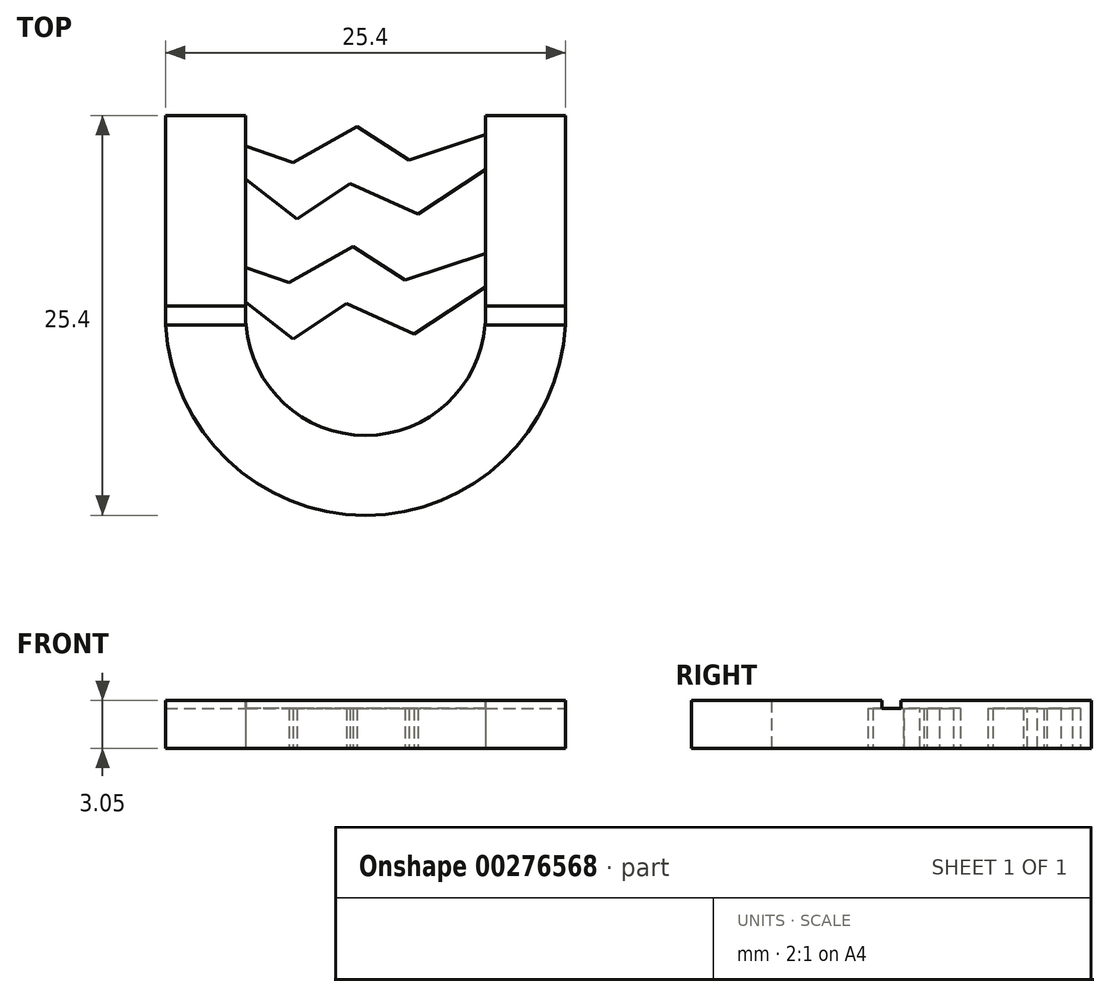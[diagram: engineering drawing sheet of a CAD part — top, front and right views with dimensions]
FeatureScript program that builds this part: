
annotation { "Feature Type Name" : "Feature", "Feature Type Description" : "" }
export const myFeature = defineFeature(function(context is Context, id is Id, definition is map)
    precondition{}
    {
        {
            var Q0;
            Q0=qCreatedBy(makeId("Top.planeOp"),FACE);
            var sketch = newSketch(context, id + "F0", { "sketchPlane" : qUnion([Q0])});
            skLineSegment(sketch, "E0.bottom", {"start": v(12.7, 12.7) * mm, "end": v(7.62, 12.7) * mm});
            skLineSegment(sketch, "E0.left", {"start": v(12.7, 12.7) * mm, "end": v(12.7, 0) * mm});
            skLineSegment(sketch, "E0.right", {"start": v(-12.7, 12.7) * mm, "end": v(-12.7, 0) * mm});
            skPoint(sketch, "E0.middle", {"position": v(0, 0) * mm});
            skArc(sketch, "E1", {"start": v(-12.7, 0) * mm, "mid": v(0, -12.7) * mm, "end": v(12.7, 0) * mm});
            skArc(sketch, "E2", {"start": v(-7.62, 0) * mm, "mid": v(0, -7.62) * mm, "end": v(7.62, 0) * mm});
            skLineSegment(sketch, "E3", {"start": v(-12.7, 0) * mm, "end": v(-12.7, 12.7) * mm});
            skLineSegment(sketch, "E4", {"start": v(0, 0) * mm, "end": v(-7.62, 0) * mm});
            skLineSegment(sketch, "E5", {"start": v(-7.62, 0) * mm, "end": v(-7.62, 12.7) * mm});
            skLineSegment(sketch, "E6", {"start": v(-7.62, 12.7) * mm, "end": v(-7.62, 0) * mm});
            skLineSegment(sketch, "E7", {"start": v(0, 0) * mm, "end": v(7.62, 0) * mm});
            skLineSegment(sketch, "E8", {"start": v(7.62, 0) * mm, "end": v(7.62, 12.7) * mm});
            skLineSegment(sketch, "E9.trimOffspring", {"start": v(-7.62, 12.7) * mm, "end": v(-12.7, 12.7) * mm});
            skPoint(sketch, "E10.orphan", {"position": v(-12.7, -12.7) * mm});
            skPoint(sketch, "E11.orphan", {"position": v(12.7, -12.7) * mm});
            skSolve(sketch);
        }
        {
            var Q0;
            Q0=makeQuery(id+"F0.imprint","IMPRINT",FACE,{"disambiguationData":[TD([[makeQuery(id+"F0.imprint","IMPRINT",EDGE,{"derivedFrom":sQuery(id+"F0.wireOp",EDGE,"E0.bottom")}),1.0]])]});
            extrude(context, id + "F1", {"entities" : qUnion([Q0]), "depth" : 3.05 * mm});
        }
        {
            var Q0;
            Q0=qCreatedBy(makeId("Top.planeOp"),FACE);
            var sketch = newSketch(context, id + "F2", { "sketchPlane" : qUnion([Q0])});
            skLineSegment(sketch, "E12", {"start": v(-8.66, 11.13) * mm, "end": v(-4.61, 9.7) * mm});
            skLineSegment(sketch, "E13", {"start": v(-4.61, 9.7) * mm, "end": v(-0.53, 12.01) * mm});
            skLineSegment(sketch, "E14", {"start": v(-0.53, 12.01) * mm, "end": v(2.77, 9.88) * mm});
            skLineSegment(sketch, "E15", {"start": v(2.77, 9.88) * mm, "end": v(8.77, 11.86) * mm});
            skLineSegment(sketch, "E16", {"start": v(8.77, 11.86) * mm, "end": v(9.61, 10.58) * mm});
            skLineSegment(sketch, "E17", {"start": v(9.61, 10.58) * mm, "end": v(3.32, 6.45) * mm});
            skLineSegment(sketch, "E18", {"start": v(3.32, 6.45) * mm, "end": v(-0.97, 8.37) * mm});
            skLineSegment(sketch, "E19", {"start": v(-0.97, 8.37) * mm, "end": v(-4.35, 6.13) * mm});
            skLineSegment(sketch, "E20", {"start": v(-4.35, 6.13) * mm, "end": v(-8.7, 9.48) * mm});
            skLineSegment(sketch, "E21", {"start": v(-8.7, 9.48) * mm, "end": v(-8.66, 11.13) * mm});
            skLineSegment(sketch, "E22", {"start": v(-8.9, 3.5) * mm, "end": v(-4.86, 2.07) * mm});
            skLineSegment(sketch, "E23", {"start": v(-4.86, 2.07) * mm, "end": v(-0.78, 4.4) * mm});
            skLineSegment(sketch, "E24", {"start": v(-0.78, 4.4) * mm, "end": v(2.52, 2.26) * mm});
            skLineSegment(sketch, "E25", {"start": v(2.52, 2.26) * mm, "end": v(8.52, 4.24) * mm});
            skLineSegment(sketch, "E26", {"start": v(8.52, 4.24) * mm, "end": v(9.36, 2.96) * mm});
            skLineSegment(sketch, "E27", {"start": v(9.36, 2.96) * mm, "end": v(3.07, -1.17) * mm});
            skLineSegment(sketch, "E28", {"start": v(3.07, -1.17) * mm, "end": v(-1.22, 0.75) * mm});
            skLineSegment(sketch, "E29", {"start": v(-1.22, 0.75) * mm, "end": v(-4.6, -1.49) * mm});
            skLineSegment(sketch, "E30", {"start": v(-4.6, -1.49) * mm, "end": v(-8.94, 1.85) * mm});
            skLineSegment(sketch, "E31", {"start": v(-8.94, 1.85) * mm, "end": v(-8.9, 3.5) * mm});
            skSolve(sketch);
        }
        {
            var Q0;
            Q0 = qSketchRegion(id + "F2", true);
            extrude(context, id + "F3", {"entities" : qUnion([Q0]), "operationType" : NewBodyOperationType.ADD, "depth" : 2.54 * mm});
        }
        {
            var Q0;
            Q0=makeQuery(id+"F1.opExtrude","CAP_FACE",FACE,{"disambiguationData":[OSD([sQuery(id+"F0.wireOp",EDGE,"E0.bottom"),sQuery(id+"F0.wireOp",EDGE,"E0.left"),sQuery(id+"F0.wireOp",EDGE,"E1"),sQuery(id+"F0.wireOp",EDGE,"E2"),sQuery(id+"F0.wireOp",EDGE,"E3"),sQuery(id+"F0.wireOp",EDGE,"E6"),sQuery(id+"F0.wireOp",EDGE,"E8"),sQuery(id+"F0.wireOp",EDGE,"E9.trimOffspring")])],"isStart":false});
            var sketch = newSketch(context, id + "F4", { "sketchPlane" : qUnion([Q0])});
            skLineSegment(sketch, "E32.bottom", {"start": v(-14.64, 0.6) * mm, "end": v(14.64, 0.6) * mm});
            skLineSegment(sketch, "E32.top", {"start": v(-14.64, -0.6) * mm, "end": v(14.64, -0.6) * mm});
            skLineSegment(sketch, "E32.left", {"start": v(-14.64, 0.6) * mm, "end": v(-14.64, -0.6) * mm});
            skLineSegment(sketch, "E32.right", {"start": v(14.64, 0.6) * mm, "end": v(14.64, -0.6) * mm});
            skPoint(sketch, "E32.middle", {"position": v(0, 0) * mm});
            skSolve(sketch);
        }
        {
            var Q0;
            Q0 = qSketchRegion(id + "F4", true);
            extrude(context, id + "F5", {"entities" : qUnion([Q0]), "operationType" : NewBodyOperationType.REMOVE, "oppositeDirection" : true, "depth" : 0.5 * mm});
        }
    });
